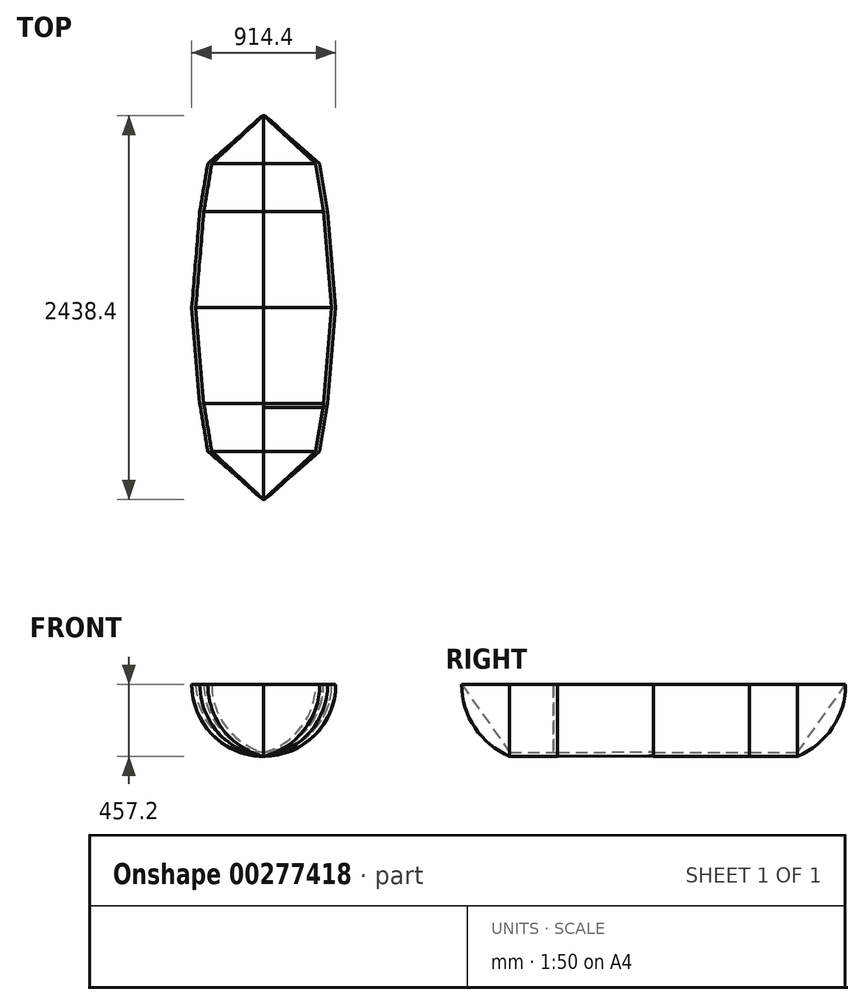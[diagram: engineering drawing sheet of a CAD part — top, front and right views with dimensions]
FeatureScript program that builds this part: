
annotation { "Feature Type Name" : "Feature", "Feature Type Description" : "" }
export const myFeature = defineFeature(function(context is Context, id is Id, definition is map)
    precondition{}
    {
        {
            var Q0;
            Q0=qCreatedBy(makeId("Top.planeOp"),FACE);
            var sketch = newSketch(context, id + "F0", { "sketchPlane" : qUnion([Q0])});
            skLineSegment(sketch, "E0", {"start": v(0, 0) * mm, "end": v(0, -1219.2) * mm});
            skLineSegment(sketch, "E1", {"start": v(0, 0) * mm, "end": v(0, 1219.2) * mm});
            skLineSegment(sketch, "E2", {"start": v(0, 0) * mm, "end": v(457.2, 0) * mm});
            skLineSegment(sketch, "E3", {"start": v(0, 0) * mm, "end": v(-457.2, 0) * mm});
            skSolve(sketch);
        }
        {
            var Q0;
            Q0=qCreatedBy(makeId("Right.planeOp"),FACE);
            var sketch = newSketch(context, id + "F1", { "sketchPlane" : qUnion([Q0])});
            skLineSegment(sketch, "E4", {"start": v(-1219.2, 0) * mm, "end": v(0, 0) * mm});
            skLineSegment(sketch, "E5", {"start": v(-1219.2, 0) * mm, "end": v(-1219.2, 457.2) * mm});
            skLineSegment(sketch, "E6", {"start": v(0, 0) * mm, "end": v(1219.2, 0) * mm});
            skLineSegment(sketch, "E7", {"start": v(1219.2, 0) * mm, "end": v(1219.2, 457.2) * mm});
            skPoint(sketch, "E8", {"position": v(-914.4, 0) * mm});
            skPoint(sketch, "E9", {"position": v(914.4, 0) * mm});
            skArc(sketch, "E10", {"start": v(-1219.2, 457.2) * mm, "mid": v(-1136.01, 182.46) * mm, "end": v(-914.4, 0) * mm});
            skArc(sketch, "E11", {"start": v(914.4, 0) * mm, "mid": v(1136.01, 182.46) * mm, "end": v(1219.2, 457.2) * mm});
            skSolve(sketch);
        }
        {
            var Q0;
            Q0=qCreatedBy(makeId("Front.planeOp"),FACE);
            cPlane(context, id + "F2", {"entities" : qUnion([Q0]), "cplaneType" : CPlaneType.OFFSET, "offset" : 609.6 * mm, "width" : 152.4 * mm, "height" : 152.4 * mm});
        }
        {
            var Q0;
            Q0=qCreatedBy(makeId("Front.planeOp"),FACE);
            cPlane(context, id + "F3", {"entities" : qUnion([Q0]), "cplaneType" : CPlaneType.OFFSET, "offset" : 609.6 * mm, "oppositeDirection" : true, "width" : 152.4 * mm, "height" : 152.4 * mm});
        }
        {
            var Q0;
            Q0=qCreatedBy(makeId("Front.planeOp"),FACE);
            cPlane(context, id + "F4", {"entities" : qUnion([Q0]), "cplaneType" : CPlaneType.OFFSET, "offset" : 914.4 * mm, "width" : 152.4 * mm, "height" : 152.4 * mm});
        }
        {
            var Q0;
            Q0=qCreatedBy(makeId("Front.planeOp"),FACE);
            cPlane(context, id + "F5", {"entities" : qUnion([Q0]), "cplaneType" : CPlaneType.OFFSET, "offset" : 914.4 * mm, "oppositeDirection" : true, "width" : 152.4 * mm, "height" : 152.4 * mm});
        }
        {
            var Q0;
            Q0=qCreatedBy(makeId("Front.planeOp"),FACE);
            var sketch = newSketch(context, id + "F6", { "sketchPlane" : qUnion([Q0])});
            skLineSegment(sketch, "E12.bottom", {"start": v(0, 0) * mm, "end": v(457.2, 0) * mm});
            skLineSegment(sketch, "E12.top", {"start": v(0, 457.2) * mm, "end": v(457.2, 457.2) * mm});
            skLineSegment(sketch, "E12.left", {"start": v(0, 0) * mm, "end": v(0, 457.2) * mm});
            skLineSegment(sketch, "E12.right", {"start": v(457.2, 0) * mm, "end": v(457.2, 457.2) * mm});
            skArc(sketch, "E13", {"start": v(0, 2.55) * mm, "mid": v(323.13, 134.81) * mm, "end": v(457.2, 457.2) * mm});
            skArc(sketch, "E14.0", {"start": v(0, 27.95) * mm, "mid": v(305.17, 152.77) * mm, "end": v(431.8, 457.2) * mm});
            skSolve(sketch);
        }
        {
            var Q0;
            Q0=qCreatedBy(makeId("Front.planeOp"),FACE);
            var sketch = newSketch(context, id + "F7", { "sketchPlane" : qUnion([Q0])});
            skLineSegment(sketch, "E15", {"start": v(457.2, 0) * mm, "end": v(457.2, 457.2) * mm});
            skLineSegment(sketch, "E16", {"start": v(-457.19, 0) * mm, "end": v(-457.19, 457.2) * mm});
            skLineSegment(sketch, "E17", {"start": v(457.2, 457.2) * mm, "end": v(0, 457.2) * mm});
            skLineSegment(sketch, "E18", {"start": v(0, 457.2) * mm, "end": v(0, 0) * mm});
            skArc(sketch, "E19", {"start": v(0, 0) * mm, "mid": v(323.29, 133.91) * mm, "end": v(457.2, 457.2) * mm});
            skArc(sketch, "E20.0", {"start": v(0, 25.4) * mm, "mid": v(305.33, 151.87) * mm, "end": v(431.8, 457.2) * mm});
            skSolve(sketch);
        }
        {
            var Q0;
            Q0=qCreatedBy(id+"F4.planeOp",FACE);
            var sketch = newSketch(context, id + "F8", { "sketchPlane" : qUnion([Q0])});
            skLineSegment(sketch, "E21", {"start": v(0, 0) * mm, "end": v(355.6, 0) * mm});
            skLineSegment(sketch, "E22", {"start": v(355.6, 457.01) * mm, "end": v(0, 457.01) * mm});
            skLineSegment(sketch, "E23", {"start": v(0, 457.01) * mm, "end": v(0, 0) * mm});
            skPoint(sketch, "E24", {"position": v(330.2, 457.01) * mm});
            skPoint(sketch, "E25", {"position": v(0, 25.4) * mm});
            skLineSegment(sketch, "E26", {"start": v(355.6, 457.01) * mm, "end": v(355.6, 0) * mm});
            skArc(sketch, "E27", {"start": v(0, 0) * mm, "mid": v(256.23, 167.48) * mm, "end": v(355.6, 457.01) * mm});
            skArc(sketch, "E28.0", {"start": v(0, 26.25) * mm, "mid": v(238.15, 185.63) * mm, "end": v(330.2, 457.01) * mm});
            skSolve(sketch);
        }
        {
            var Q0;
            Q0=qCreatedBy(id+"F2.planeOp",FACE);
            var sketch = newSketch(context, id + "F9", { "sketchPlane" : qUnion([Q0])});
            skLineSegment(sketch, "E29", {"start": v(406.4, 0) * mm, "end": v(406.4, 457.2) * mm});
            skLineSegment(sketch, "E30", {"start": v(406.4, 457.2) * mm, "end": v(0, 457.2) * mm});
            skLineSegment(sketch, "E31", {"start": v(0, 457.2) * mm, "end": v(0, 0) * mm});
            skArc(sketch, "E32", {"start": v(0, 0) * mm, "mid": v(290.11, 151.34) * mm, "end": v(406.4, 457.2) * mm});
            skArc(sketch, "E33.0", {"start": v(0, 25.59) * mm, "mid": v(272.12, 169.34) * mm, "end": v(381, 457.2) * mm});
            skSolve(sketch);
        }
        {
            var Q0;
            Q0=qCreatedBy(id+"F5.planeOp",FACE);
            var sketch = newSketch(context, id + "F10", { "sketchPlane" : qUnion([Q0])});
            skLineSegment(sketch, "E34", {"start": v(355.42, -0.23) * mm, "end": v(355.42, 456.97) * mm});
            skLineSegment(sketch, "E35", {"start": v(355.42, 456.97) * mm, "end": v(0, 456.97) * mm});
            skLineSegment(sketch, "E36", {"start": v(0, 456.97) * mm, "end": v(0, 0) * mm});
            skArc(sketch, "E37", {"start": v(0, 0) * mm, "mid": v(256.1, 167.51) * mm, "end": v(355.42, 456.97) * mm});
            skPoint(sketch, "E38", {"position": v(330.02, 456.97) * mm});
            skPoint(sketch, "E39", {"position": v(0, 25.4) * mm});
            skArc(sketch, "E40", {"start": v(0, 25.4) * mm, "mid": v(238.29, 185.15) * mm, "end": v(330.02, 456.97) * mm});
            skSolve(sketch);
        }
        {
            var Q0;
            Q0=qCreatedBy(id+"F3.planeOp",FACE);
            var sketch = newSketch(context, id + "F11", { "sketchPlane" : qUnion([Q0])});
            skLineSegment(sketch, "E41", {"start": v(0, 0) * mm, "end": v(406.4, 0) * mm});
            skLineSegment(sketch, "E42", {"start": v(406.4, 0) * mm, "end": v(406.4, 457.2) * mm});
            skLineSegment(sketch, "E43", {"start": v(406.4, 457.2) * mm, "end": v(0, 457.2) * mm});
            skLineSegment(sketch, "E44", {"start": v(0, 457.2) * mm, "end": v(0, 0) * mm});
            skArc(sketch, "E45", {"start": v(0, 0) * mm, "mid": v(290.11, 151.34) * mm, "end": v(406.4, 457.2) * mm});
            skPoint(sketch, "E46", {"position": v(381, 457.2) * mm});
            skPoint(sketch, "E47", {"position": v(0, 25.4) * mm});
            skArc(sketch, "E48.0", {"start": v(0, 25.59) * mm, "mid": v(272.12, 169.34) * mm, "end": v(381, 457.2) * mm});
            skSolve(sketch);
        }
        {
            var Q0;
            Q0=sQuery(id+"F1.wireOp",VERTEX,"E10.start");
            var Q1;
            {var subQ0=sQuery(id+"F8.wireOp",EDGE,"E27");Q1=makeQuery(id+"F8.imprint","IMPRINT",FACE,{"disambiguationData":[TD([[makeQuery(id+"F8.imprint","IMPRINT",EDGE,{"derivedFrom":subQ0}),1.0]])]});}
            var Q2;
            Q2=sQuery(id+"F1.wireOp",EDGE,"E10");
            loft(context, id + "F12", {"addGuides" : true, "sheetProfilesArray" : [{ "sheetProfileEntities" : qUnion([Q0]) }, { "sheetProfileEntities" : qUnion([Q1]) }], "guidesArray" : [{ "guideEntities" : qUnion([Q2]), "guideDerivativeType" : LoftGuideDerivativeType.DEFAULT, "guideDerivativeMagnitude" : 1 }]});
        }
        {
            var Q1;
            {var subQ0=sQuery(id+"F8.wireOp",EDGE,"E27");Q1=makeQuery(id+"F8.imprint","IMPRINT",FACE,{"disambiguationData":[TD([[makeQuery(id+"F8.imprint","IMPRINT",EDGE,{"derivedFrom":subQ0}),1.0]])]});}
            var Q2;
            {var subQ0=sQuery(id+"F9.wireOp",EDGE,"E32");Q2=makeQuery(id+"F9.imprint","IMPRINT",FACE,{"disambiguationData":[TD([[makeQuery(id+"F9.imprint","IMPRINT",EDGE,{"derivedFrom":subQ0}),1.0]])]});}
            loft(context, id + "F13", {"operationType" : NewBodyOperationType.ADD, "sheetProfilesArray" : [{ "sheetProfileEntities" : qUnion([Q1]) }, { "sheetProfileEntities" : qUnion([Q2]) }]});
        }
        {
            var Q1;
            {var subQ0=sQuery(id+"F9.wireOp",EDGE,"E32");Q1=makeQuery(id+"F13.opLoft","CAP_FACE",FACE,{"disambiguationData":[OSD([makeQuery(id+"F9.imprint","IMPRINT",FACE,{"disambiguationData":[TD([[makeQuery(id+"F9.imprint","IMPRINT",EDGE,{"derivedFrom":subQ0}),1.0]])]})])],"isStart":true});}
            var Q2;
            {var subQ0=sQuery(id+"F6.wireOp",EDGE,"E13");Q2=makeQuery(id+"F6.imprint","IMPRINT",FACE,{"disambiguationData":[TD([[makeQuery(id+"F6.imprint","IMPRINT",EDGE,{"derivedFrom":subQ0}),1.0]])]});}
            loft(context, id + "F14", {"operationType" : NewBodyOperationType.ADD, "sheetProfilesArray" : [{ "sheetProfileEntities" : qUnion([Q1]) }, { "sheetProfileEntities" : qUnion([Q2]) }]});
        }
        {
            var Q1;
            {var subQ0=sQuery(id+"F7.wireOp",EDGE,"E19");Q1=makeQuery(id+"F7.imprint","IMPRINT",FACE,{"disambiguationData":[TD([[makeQuery(id+"F7.imprint","IMPRINT",EDGE,{"derivedFrom":subQ0}),1.0]])]});}
            var Q2;
            {var subQ0=sQuery(id+"F11.wireOp",EDGE,"E45");Q2=makeQuery(id+"F11.imprint","IMPRINT",FACE,{"disambiguationData":[TD([[makeQuery(id+"F11.imprint","IMPRINT",EDGE,{"derivedFrom":subQ0}),1.0]])]});}
            loft(context, id + "F15", {"operationType" : NewBodyOperationType.ADD, "sheetProfilesArray" : [{ "sheetProfileEntities" : qUnion([Q1]) }, { "sheetProfileEntities" : qUnion([Q2]) }]});
        }
        {
            var Q1;
            {var subQ0=sQuery(id+"F11.wireOp",EDGE,"E45");Q1=makeQuery(id+"F11.imprint","IMPRINT",FACE,{"disambiguationData":[TD([[makeQuery(id+"F11.imprint","IMPRINT",EDGE,{"derivedFrom":subQ0}),1.0]])]});}
            var Q2;
            {var subQ0=sQuery(id+"F10.wireOp",EDGE,"E37");Q2=makeQuery(id+"F10.imprint","IMPRINT",FACE,{"disambiguationData":[TD([[makeQuery(id+"F10.imprint","IMPRINT",EDGE,{"derivedFrom":subQ0}),1.0]])]});}
            loft(context, id + "F16", {"operationType" : NewBodyOperationType.ADD, "sheetProfilesArray" : [{ "sheetProfileEntities" : qUnion([Q1]) }, { "sheetProfileEntities" : qUnion([Q2]) }]});
        }
        {
            var Q1;
            {var subQ0=sQuery(id+"F10.wireOp",EDGE,"E37");Q1=makeQuery(id+"F10.imprint","IMPRINT",FACE,{"disambiguationData":[TD([[makeQuery(id+"F10.imprint","IMPRINT",EDGE,{"derivedFrom":subQ0}),1.0]])]});}
            var Q2;
            Q2=sQuery(id+"F1.wireOp",VERTEX,"E11.end");
            var Q3;
            Q3=sQuery(id+"F1.wireOp",EDGE,"E11");
            loft(context, id + "F17", {"operationType" : NewBodyOperationType.ADD, "addGuides" : true, "sheetProfilesArray" : [{ "sheetProfileEntities" : qUnion([Q1]) }, { "sheetProfileEntities" : qUnion([Q2]) }], "guidesArray" : [{ "guideEntities" : qUnion([Q3]), "guideDerivativeType" : LoftGuideDerivativeType.DEFAULT, "guideDerivativeMagnitude" : 1 }]});
        }
        {
            var Q0;
            {var subQ0=sQuery(id+"F8.wireOp",EDGE,"E27");Q0=makeQuery(id+"F12.opLoft","SWEPT_BODY",BODY,{"disambiguationData":[OSD([sQuery(id+"F1.wireOp",VERTEX,"E10.start"),sQuery(id+"F1.wireOp",EDGE,"E10"),makeQuery(id+"F8.imprint","IMPRINT",FACE,{"disambiguationData":[TD([[makeQuery(id+"F8.imprint","IMPRINT",EDGE,{"derivedFrom":subQ0}),1.0]])]})])]});}
            var Q1;
            Q1=qCreatedBy(makeId("Right.planeOp"),FACE);
            mirror(context, id + "F18", {"operationType" : NewBodyOperationType.ADD, "entities" : qUnion([Q0]), "mirrorPlane" : qUnion([Q1])});
        }
        {
            var Q0;
            {var subQ3=sQuery(id+"F8.wireOp",EDGE,"E28.0");Q0=makeQuery(id+"F8.imprint","IMPRINT",FACE,{"disambiguationData":[TD([[makeQuery(id+"F8.imprint","IMPRINT",EDGE,{"derivedFrom":subQ3}),1.0]])]});}
            extrude(context, id + "F19", {"entities" : qUnion([Q0]), "operationType" : NewBodyOperationType.ADD, "endBound" : BoundingType.UP_TO_NEXT, "depth" : 25.4 * mm});
        }
        {
            var Q0;
            {var subQ3=sQuery(id+"F9.wireOp",EDGE,"E33.0");Q0=makeQuery(id+"F9.imprint","IMPRINT",FACE,{"disambiguationData":[TD([[makeQuery(id+"F9.imprint","IMPRINT",EDGE,{"derivedFrom":subQ3}),1.0]])]});}
            extrude(context, id + "F20", {"entities" : qUnion([Q0]), "operationType" : NewBodyOperationType.ADD, "depth" : 25.4 * mm});
        }
    });
